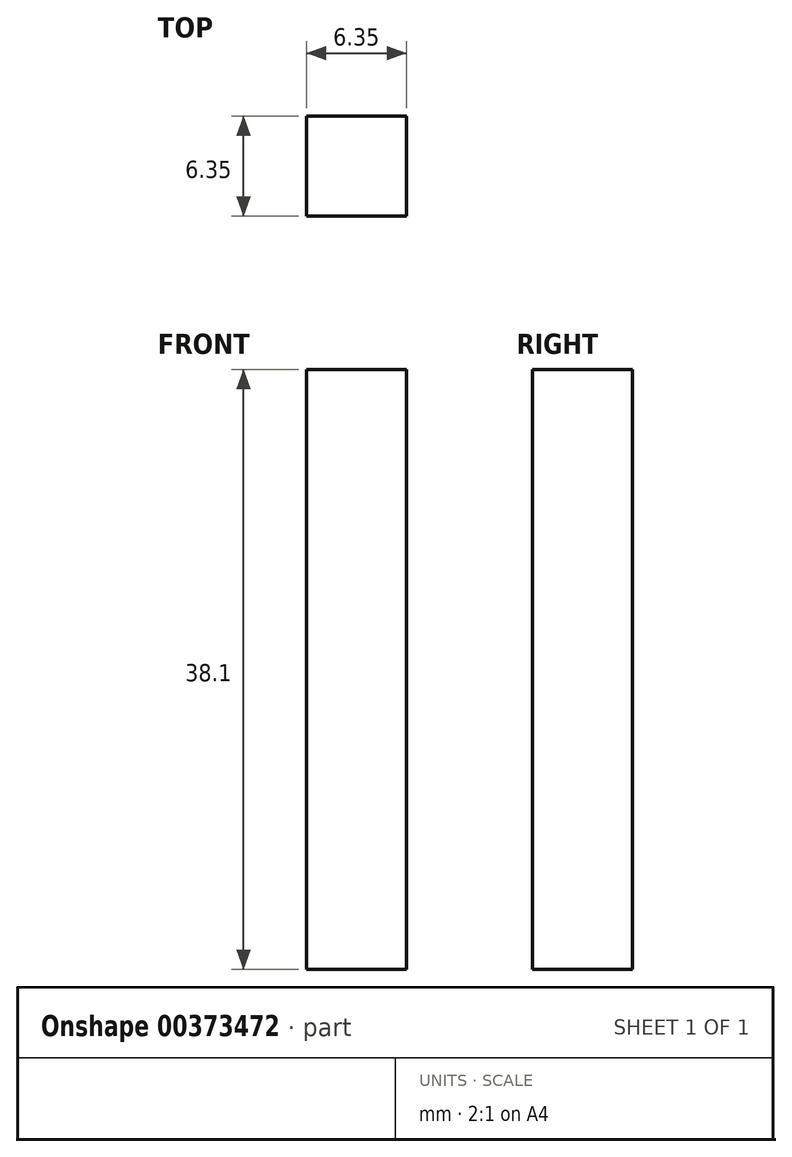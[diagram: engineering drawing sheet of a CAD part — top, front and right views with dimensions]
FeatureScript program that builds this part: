
annotation { "Feature Type Name" : "Feature", "Feature Type Description" : "" }
export const myFeature = defineFeature(function(context is Context, id is Id, definition is map)
    precondition{}
    {
        {
            var Q0;
            Q0=qCreatedBy(makeId("Front.planeOp"),FACE);
            var sketch = newSketch(context, id + "F0", { "sketchPlane" : qUnion([Q0])});
            skLineSegment(sketch, "E0", {"start": v(-56.9, 13.8) * mm, "end": v(-56.9, -24.3) * mm});
            skLineSegment(sketch, "E1", {"start": v(-56.9, -24.3) * mm, "end": v(-50.55, -24.3) * mm});
            skLineSegment(sketch, "E2", {"start": v(-56.9, 13.8) * mm, "end": v(-50.55, 13.8) * mm});
            skLineSegment(sketch, "E3", {"start": v(-50.55, 13.8) * mm, "end": v(-50.55, -24.3) * mm});
            skSolve(sketch);
        }
        {
            var Q0;
            Q0=makeQuery(id+"F0.imprint","IMPRINT",FACE,{"disambiguationData":[TD([[makeQuery(id+"F0.imprint","IMPRINT",EDGE,{"derivedFrom":sQuery(id+"F0.wireOp",EDGE,"E0")}),1.0]])]});
            extrude(context, id + "F1", {"entities" : qUnion([Q0]), "depth" : 6.35 * mm});
        }
    });
